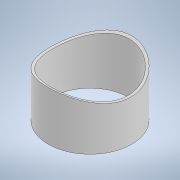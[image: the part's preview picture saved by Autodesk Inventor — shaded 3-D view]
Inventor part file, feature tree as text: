
AUTODESK INVENTOR PART (.ipt)
format: ipt  version: 2021 (Build 250183000, 183)  size: 112,128 bytes
history: native  units: mm
features: extrude x2, sketch x2
ambient origin geometry x8: Origin, YZ Plane, XZ Plane, XY Plane, X Axis, Y Axis, Z Axis, Center Point
bodies: Solid1 (feature_tree)
feature tree (4):
  extrude  "Extrusion1"  Depth=60.0mm
  extrude  "Extrusion2"  Depth=150.0mm
  sketch  "Sketch1"  dims[d0=64.0mm d1=60.0mm]
  sketch  "Sketch2"  dims[d2=40.0mm d3=0.0mm d4=150.0mm d5=0.0mm d6=0.0mm]
